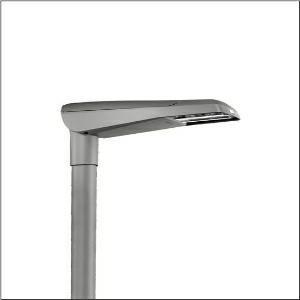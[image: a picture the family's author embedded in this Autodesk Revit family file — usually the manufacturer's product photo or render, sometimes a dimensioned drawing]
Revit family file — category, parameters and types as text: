
# Revit family: streetlight_sl_11_iq_micro___p1_0a_5xc1c51e08ce_6305
name_source: partatom
category: Lighting Fixtures
units: mm (PartAtom-declared; Revit-internal decimal feet)

## family parameters
Cut with Voids When Loaded = No
Host = Face
Light Source = No
Part Type = Normal
Room Calculation Point = No
Round Connector Dimension = Use Diameter
Shared = No

## types (1)
- --- (1 x LED, 1600 lm, 10.8 W, 3000K)
    Apparent Load = 11 VA
    CIE Flux Codes = 29 63 93 100 100
    Color Rendering = 70
    Color Temperature = 3000K
    Default Elevation = 1800 mm
    Description = Streetlight SL 11 iQ micro, mast luminaire, primary light control with 3 zone facetted reflector, of plastic, silver coated, highly specular, primary optical cover: cover, of PMMA, transparent, light distribution: P1.0a, light emission: direct distribution, primary light characteristic: asymmetric, installation type: post-top, side-entry, lamps: LED, High Power LED, rated values: 1.600lm | 10,8W | 148,1lm/W (begin service life); end service life: 1.600lm | 11,1W; at 50% lumin. flux: 800lm | 6W | 133,3lm/W, colour temperature: 3000K, colour rendering: CRI > 70, light colour: 730, light setting 1 begin service life: 100% | 1.600lm | 10,8W | 148,1lm/W | 3.000K, light setting 1 end service life: 11,1W, further light settings possible, control: optimised constant luminous flux control (CLO 2.0), Desk-Remote (wireless, voltage-free reading and setting of iQ features in the workshop via application-optimized NFC function/RFID function), Light-Fading, Smart-Wire, Night-Set, Lumen-Switch, Temp-Guard, Auto-Match, with cable H07RN-F 5x 1.5mm², mains connection: 230..240V, AC, 50/60Hz, connection cable pre-assembled, cable length: 5,5m, luminaire housing, of diecast aluminium, powder-coated, Siteco® metallic grey (DB 702S), please order mast flange separately, inclination adjustable without tools: 0°, 5°, 10°, 15° (post-top) | 0°, -5°, -10°, -15° (side-entry), sealing non-destructively replaceable, multi-level sealing system, length: 600mm, width: 174mm, height: 116mm, mast flange for spigot size: 42mm (side-entry): 5XC10008XM4, 60/48mm (side-entry/post-top): 5XC10108XM2, 76/60mm (side-entry/post-top): 5XC10108XM1, equipment: standard, protection rating (complete): IP66, insulation class (complete): insulation class II (safety insulation), certification: CE, ENEC, ENEC+, VDE, impact resistance: IK10, permissible operating ambient temperature for outdoor applications: -25..+50°C, standard-compliant lighting for roads and squares, Environmental Product Declaration (EPD) tested and certified by an independent institute, packaging unit: 1 piece

Light Distribution: P1.0a
    Height = 116 mm
    Lamp = 1 x LED
    Lamp Light Flux = 1600 lm
    Lamp Power = 10.8 W
    Lamp count = 1
    Length = 600 mm
    Luminous efficacy = 148 lm/W
    Manufacturer = Siteco
    ModVariant = No
    Model = 5XC1C51E08CE
    Number of Poles = 1
    OnlyDefault = Yes
    Power Factor = 1
    Product Name = Streetlight SL 11 iQ micro | P1.0a
    Product group = mast luminaire | pylon top
    ProductGroupID = 6100
    Protection Class = Protection class II
    Protection Degree = IP 66
    RLX_Detail_Level = 1
    RLX_Emergency_Light_Flux = 0 lm
    RLX_Emergency_Type = 0
    RLX_Emergency_Type_DB = No
    RlxData = <blob elided: 26649 chars, md5=4552725b>
    Socket = socket
    Standby Power = 0 W
    System Light Flux = 1600 lm
    System Power = 11 W
    Type Comments = factory setting: luminous flux: 100 % | dim-lin: 254 | 194 mA
    Type Image = l_1006566.jpg
    URL = http://relux.com
    VarID = @adj_018181
    Voltage = 0 V
    Weight = 0.00 kg
    Width = 174 mm

## geometry (parser evidence)
native form markers: Blend x4, Sweep x10
no freeform markers — native parametric forms only
